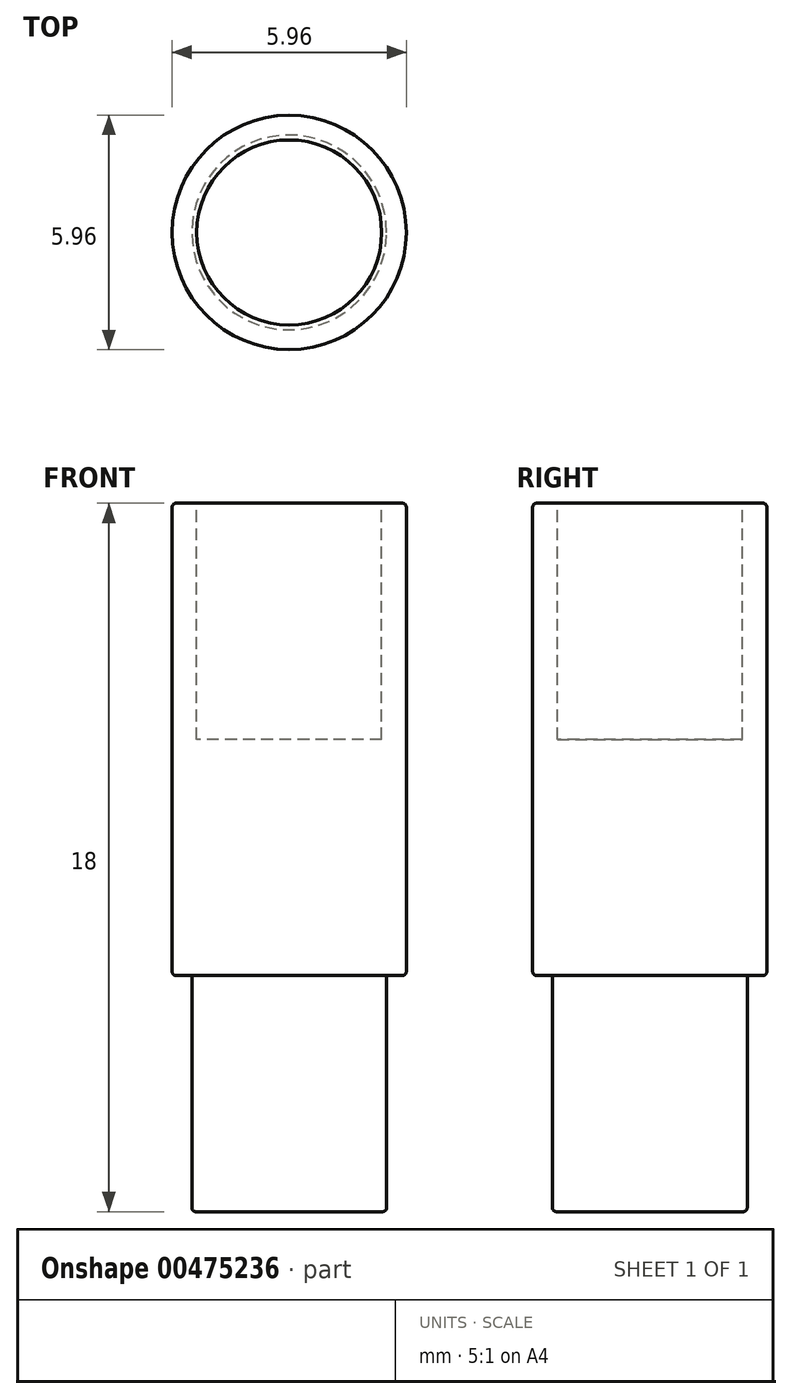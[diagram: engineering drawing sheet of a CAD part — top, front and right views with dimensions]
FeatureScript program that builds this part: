
annotation { "Feature Type Name" : "Feature", "Feature Type Description" : "" }
export const myFeature = defineFeature(function(context is Context, id is Id, definition is map)
    precondition{}
    {
        {
            var Q0;
            Q0=qCreatedBy(makeId("Top.planeOp"),FACE);
            var sketch = newSketch(context, id + "F0", { "sketchPlane" : qUnion([Q0])});
            skCircle(sketch, "E0", {"center": v(0, 0) * mm, "radius": 2.48 * mm});
            skSolve(sketch);
        }
        {
            var Q0;
            Q0 = qSketchRegion(id + "F0", true);
            extrude(context, id + "F1", {"entities" : qUnion([Q0]), "depth" : 6 * mm});
        }
        {
            var Q0;
            Q0=makeQuery(id+"F1.opExtrude","CAP_FACE",FACE,{"disambiguationData":[OSD([sQuery(id+"F0.wireOp",EDGE,"E0")])],"isStart":false});
            var sketch = newSketch(context, id + "F2", { "sketchPlane" : qUnion([Q0])});
            skCircle(sketch, "E1", {"center": v(0, 0) * mm, "radius": 2.98 * mm});
            skSolve(sketch);
        }
        {
            var Q0;
            Q0 = qSketchRegion(id + "F2", true);
            extrude(context, id + "F3", {"entities" : qUnion([Q0]), "operationType" : NewBodyOperationType.ADD, "depth" : 12 * mm});
        }
        {
            var Q0;
            Q0=makeQuery(id+"F3.opExtrude","CAP_FACE",FACE,{"disambiguationData":[OSD([sQuery(id+"F2.wireOp",EDGE,"E1")])],"isStart":false});
            var sketch = newSketch(context, id + "F4", { "sketchPlane" : qUnion([Q0])});
            skCircle(sketch, "E2", {"center": v(0, 0) * mm, "radius": 2.35 * mm});
            skSolve(sketch);
        }
        {
            var Q0;
            Q0 = qSketchRegion(id + "F4", true);
            extrude(context, id + "F5", {"entities" : qUnion([Q0]), "operationType" : NewBodyOperationType.REMOVE, "oppositeDirection" : true, "depth" : 6 * mm});
        }
        {
            var Q0;
            Q0=makeQuery(id+"F1.opExtrude","CAP_EDGE",EDGE,{"disambiguationData":[OSD([sQuery(id+"F0.wireOp",EDGE,"E0")])],"isStart":true});
            var Q1;
            Q1=makeQuery(id+"F3.opExtrude","CAP_EDGE",EDGE,{"disambiguationData":[OSD([sQuery(id+"F2.wireOp",EDGE,"E1")])],"isStart":false});
            var Q2;
            Q2=makeQuery(id+"F5.boolean.opBoolean","COPY",EDGE,{"derivedFrom":makeQuery(id+"F5.opExtrude","CAP_EDGE",EDGE,{"disambiguationData":[OSD([sQuery(id+"F4.wireOp",EDGE,"E2")])],"isStart":true})});
            var Q3;
            Q3=makeQuery(id+"F3.opExtrude","CAP_EDGE",EDGE,{"disambiguationData":[OSD([sQuery(id+"F2.wireOp",EDGE,"E1")])],"isStart":true});
            var Q4;
            Q4=makeQuery(id+"F1.opExtrude","CAP_EDGE",EDGE,{"disambiguationData":[OSD([sQuery(id+"F0.wireOp",EDGE,"E0")])],"isStart":false});
            fillet(context, id + "F6", {"entities" : qUnion([Q0, Q1, Q2, Q3, Q4]), "radius" : .1 * mm, "tangentPropagation" : true, "allowEdgeOverflow" : false});
        }
    });
